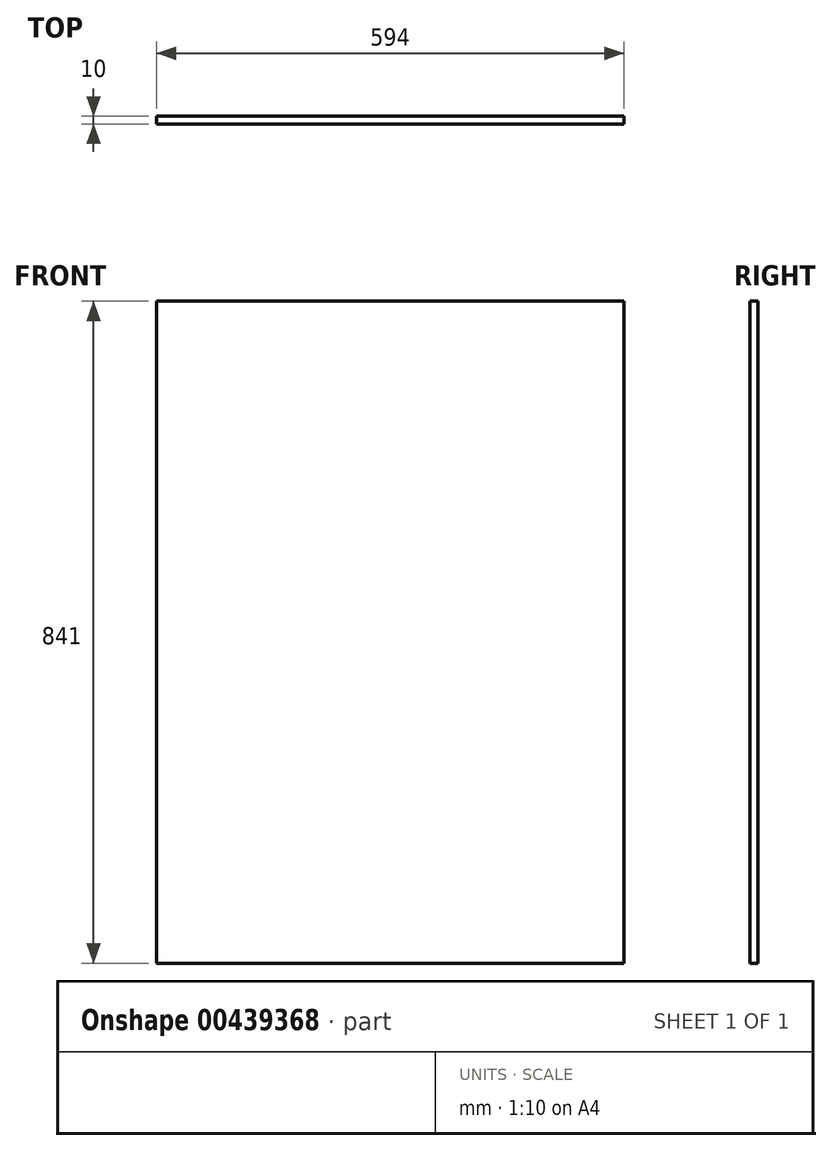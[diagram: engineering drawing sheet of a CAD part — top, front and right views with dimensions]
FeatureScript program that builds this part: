
annotation { "Feature Type Name" : "Feature", "Feature Type Description" : "" }
export const myFeature = defineFeature(function(context is Context, id is Id, definition is map)
    precondition{}
    {
        {
            var Q0;
            Q0=qCreatedBy(makeId("Front.planeOp"),FACE);
            var sketch = newSketch(context, id + "F0", { "sketchPlane" : qUnion([Q0])});
            skLineSegment(sketch, "E0.bottom", {"start": v(297, 420.5) * mm, "end": v(-297, 420.5) * mm});
            skLineSegment(sketch, "E0.top", {"start": v(297, -420.5) * mm, "end": v(-297, -420.5) * mm});
            skLineSegment(sketch, "E0.left", {"start": v(297, 420.5) * mm, "end": v(297, -420.5) * mm});
            skLineSegment(sketch, "E0.right", {"start": v(-297, 420.5) * mm, "end": v(-297, -420.5) * mm});
            skPoint(sketch, "E0.middle", {"position": v(0, 0) * mm});
            skSolve(sketch);
        }
        {
            var Q0;
            Q0=makeQuery(id+"F0.imprint","IMPRINT",FACE,{"disambiguationData":[TD([[makeQuery(id+"F0.imprint","IMPRINT",EDGE,{"derivedFrom":sQuery(id+"F0.wireOp",EDGE,"E0.bottom")}),1.0]])]});
            extrude(context, id + "F1", {"entities" : qUnion([Q0]), "depth" : 10 * mm});
        }
    });
